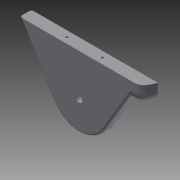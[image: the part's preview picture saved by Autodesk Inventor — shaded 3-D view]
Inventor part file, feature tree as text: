
AUTODESK INVENTOR PART (.ipt)
format: ipt  version: 2015 (Build 190159000, 159)  size: 197,120 bytes
history: native  units: mm
features: extrude x5, sketch x5, fillet x3
ambient origin geometry x8: Origin, YZ Plane, XZ Plane, XY Plane, X Axis, Y Axis, Z Axis, Center Point
bodies: Solid1 (feature_tree)
feature tree (13):
  extrude  "Extrusion1"  Depth=50.0mm
  extrude  "Extrusion2"  Depth=6.0mm
  extrude  "Extrusion3"  Depth=2.0mm
  extrude  "Extrusion4"  Depth=10.0mm TaperAngle=0.0deg
  extrude  "Extrusion5"  Depth=10.0mm
  fillet  "Fillet1"  Radius=10.0mm
  fillet  "Fillet2"  Radius=6.4mm
  fillet  "Fillet3"  Radius=48.5mm
  sketch  "Sketch1"  dims[d4=50.0mm d5=50.0mm]
  sketch  "Sketch2"  dims[d6=100.0mm d7=6.0mm]
  sketch  "Sketch3"  dims[d8=10.0mm d9=0.0mm d11=2.0mm]
  sketch  "Sketch4"  dims[d12=2.0mm d13=10.0mm d14=0.0mm]
  sketch  "Sketch5"  dims[d15=15.0mm d16=10.0mm d17=10.0mm d18=0.0mm d19=6.4mm d20=0.0mm d21=48.5mm d22=90.0deg d24=15.0mm d25=0.0mm d26=8.0mm d27=2.0mm d28=0.2mm]
